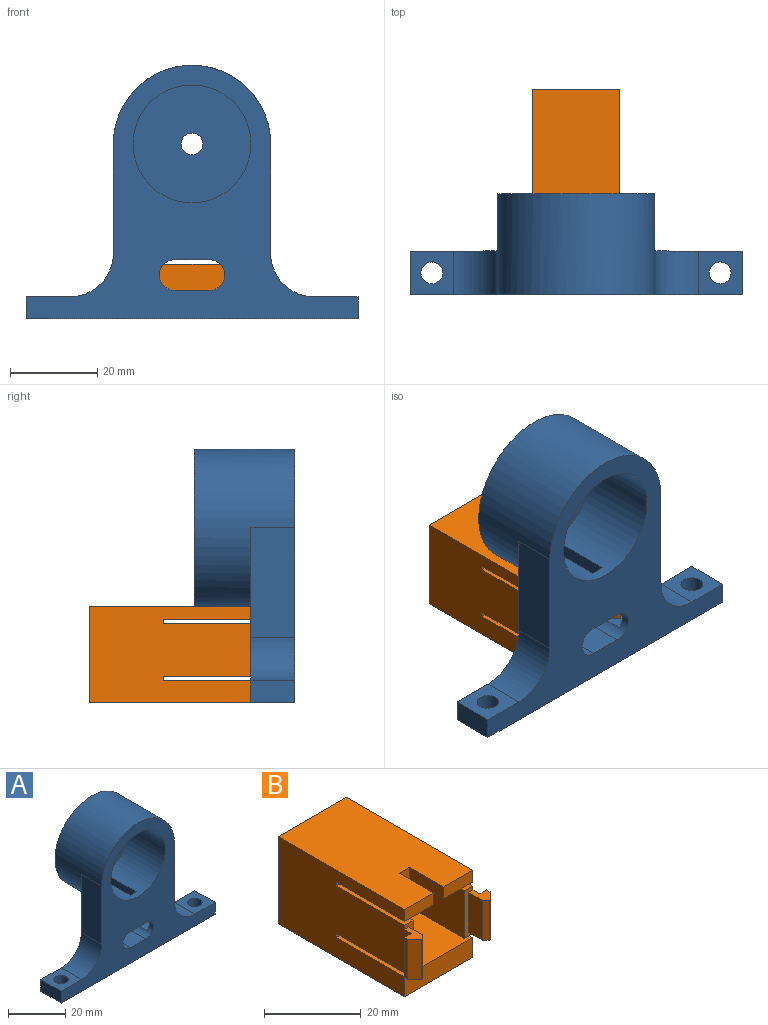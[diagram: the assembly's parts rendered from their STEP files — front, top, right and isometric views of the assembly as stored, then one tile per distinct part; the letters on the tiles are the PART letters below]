
ASSEMBLY  parts=2 mates=1
PART A: 45 faces, bbox 76x23x58 mm
  f0: plane 12.06x6mm, normal (1,0,0), area 72.4mm2, adj f1,f31,f33,f42
  f1: plane 8x5.5mm, normal (0,0,-1), area 42.5mm2, adj f0,f3,f32,f33,f42,f43,f44
  f2: plane 8x5.5mm, normal (0,0,1), area 42.5mm2, adj f3,f34,f37,f38,f39,f40,f41
  f3: plane 76x40mm, normal (0,1,0), area 951.5mm2, adj f1,f2,f4,f5,f6,f7,f8,f9
  f4: plane 76x10mm, normal (0,0,-1), area 720.7mm2, adj f3,f5,f15,f16,f26,f27
  f5: plane 10x5mm, normal (1,0,0), area 50mm2, adj f3,f4,f6,f16
  f6: plane 10x10mm, normal (0,0,1), area 80.4mm2, adj f3,f5,f16,f27,f28
  f7: plane 25x10mm, normal (1,0,0), area 250mm2, adj f3,f16,f17,f28
  f8: plane 25x10mm, normal (-1,0,0), area 250mm2, adj f3,f16,f17,f29
  f9: plane 10x10mm, normal (0,0,1), area 80.4mm2, adj f3,f15,f16,f26,f29
  f10: cylinder r=3.5mm len=10mm, axis (0,-1,0), area 68.4mm2, adj f3,f11,f13,f16,f30,f32,f33
  f11: plane 10x8mm, normal (0,0,-1), area 80mm2, adj f3,f10,f12,f16
  f12: cylinder r=3.5mm len=10mm, axis (0,-1,0), area 68.4mm2, adj f3,f11,f13,f16,f34,f35,f38
  f13: plane 10x7.64mm, normal (0,0,1), area 76.4mm2, adj f3,f10,f12,f16
  f14: cylinder r=13.5mm len=27mm, axis (0,-1,0), area 1481.7mm2, adj f16,f18,f20,f21,f22,f23
  f15: plane 10x5mm, normal (-1,0,0), area 50mm2, adj f3,f4,f9,f16
  f16: plane 76x58mm, normal (0,-1,0), area 1524.9mm2, adj f4,f5,f6,f7,f8,f9,f10,f11
  f17: cylinder r=18mm len=36mm, axis (0,1,0), area 2013.2mm2, adj f3,f7,f8,f16,f20,f21,f22,f24
  f18: plane 5.27x3mm, normal (0,1,0), area 15.6mm2, adj f14,f19,f20,f21
  f19: plane 7.5x3mm, normal (0,0,1), area 22.5mm2, adj f3,f18,f20,f21
  f20: plane 15x5.27mm, normal (-1,0,0), area 73.4mm2, adj f3,f14,f17,f18,f19,f22
  f21: plane 15x5.27mm, normal (1,0,0), area 73.4mm2, adj f3,f14,f17,f18,f19,f22
  f22: plane 4.58x3mm, normal (0,-1,0), area 13.5mm2, adj f14,f17,f20,f21
  f23: plane 27x27mm, normal (0,-1,0), area 552.9mm2, adj f14,f25
  f24: plane 36x36mm, normal (0,1,0), area 998.2mm2, adj f17,f25
  f25: cylinder r=2.5mm len=5mm, axis (0,1,0), area 78.5mm2, adj f23,f24
  f26: cylinder r=2.5mm len=5mm, axis (0,0,1), area 78.5mm2, adj f4,f9
  f27: cylinder r=2.5mm len=5mm, axis (0,0,1), area 78.5mm2, adj f4,f6
  f28: cylinder r=10mm len=10mm, axis (0,-1,0), area 157.1mm2, adj f3,f6,f7,f16
  f29: cylinder r=10mm len=10mm, axis (0,-1,0), area 157.1mm2, adj f3,f8,f9,f16
  f30: plane 8x1.55mm, normal (-1,0,0), area 12.4mm2, adj f3,f10,f31,f33
  f31: plane 8x5.5mm, normal (0,0,1), area 42.5mm2, adj f0,f3,f30,f33,f42,f43,f44
  f32: plane 8x5.61mm, normal (-1,0,0), area 44.9mm2, adj f1,f3,f10,f33
  f33: plane 12.06x5.5mm, normal (0,1,0), area 63mm2, adj f0,f1,f10,f30,f31,f32
  f34: plane 8x1.55mm, normal (1,0,0), area 12.4mm2, adj f2,f3,f12,f38
  f35: plane 8x5.61mm, normal (1,0,0), area 44.9mm2, adj f3,f12,f36,f38
  f36: plane 8x5.5mm, normal (0,0,-1), area 42.5mm2, adj f3,f35,f37,f38,f39,f40,f41
  f37: plane 12.06x6mm, normal (-1,0,0), area 72.4mm2, adj f2,f36,f38,f39
  f38: plane 12.06x5.5mm, normal (0,1,0), area 63mm2, adj f2,f12,f34,f35,f36,f37
  f39: plane 12.06x1mm, normal (0,-1,0), area 12.1mm2, adj f2,f36,f37,f40
  f40: plane 12.06x1mm, normal (-1,0,0), area 12.1mm2, adj f2,f36,f39,f41
  f41: plane 12.06x1mm, normal (-0.71,0.71,0), area 17.1mm2, adj f2,f3,f36,f40
  f42: plane 12.06x1mm, normal (0,-1,0), area 12.1mm2, adj f0,f1,f31,f43
  f43: plane 12.06x1mm, normal (1,0,0), area 12.1mm2, adj f1,f31,f42,f44
  f44: plane 12.06x1mm, normal (0.71,0.71,0), area 17.1mm2, adj f1,f3,f31,f43
PART B: 46 faces, bbox 24x42x22.1 mm
  f0: plane 35x14.06mm, normal (1,0,0), area 452.2mm2, adj f4,f20,f23,f24,f35,f36,f38,f39
  f1: plane 39x22.06mm, normal (-1,0,0), area 796.4mm2, adj f4,f7,f12,f21,f22,f23,f24,f25
  f2: plane 39x22.06mm, normal (1,0,0), area 796.4mm2, adj f5,f6,f15,f21,f22,f23,f24,f25
  f3: plane 35x14.06mm, normal (-1,0,0), area 452.2mm2, adj f5,f20,f23,f24,f40,f41,f43,f44
  f4: plane 12.06x2.5mm, normal (0,-1,0), area 17.6mm2, adj f0,f1,f8,f34,f36,f37,f39
  f5: plane 12.06x2.5mm, normal (0,-1,0), area 17.6mm2, adj f2,f3,f10,f41,f42,f44,f45
  f6: plane 8.5x3mm, normal (0,-1,0), area 25.5mm2, adj f2,f22,f23,f29
  f7: plane 8.5x3mm, normal (0,-1,0), area 25.5mm2, adj f1,f22,f23,f27
  f8: plane 10.06x4mm, normal (1,0,0), area 40.3mm2, adj f4,f19,f34,f37
  f9: plane 10.06x0.25mm, normal (0,-1,0), area 2.5mm2, adj f14,f19,f34,f37
  f10: plane 10.06x4mm, normal (-1,0,0), area 40.3mm2, adj f5,f18,f42,f45
  f11: plane 10.06x0.25mm, normal (0,-1,0), area 2.5mm2, adj f17,f18,f42,f45
  f12: plane 10.06x2mm, normal (0,1,0), area 20.1mm2, adj f1,f13,f34,f37
  f13: plane 10.06x1mm, normal (-1,0,0), area 10.1mm2, adj f12,f14,f34,f37
  f14: plane 10.06x2mm, normal (-0.71,-0.71,0), area 28.5mm2, adj f9,f13,f34,f37
  f15: plane 10.06x2mm, normal (0,1,0), area 20.1mm2, adj f2,f16,f42,f45
  f16: plane 10.06x1mm, normal (1,0,0), area 10.1mm2, adj f15,f17,f42,f45
  f17: plane 10.06x2mm, normal (0.71,-0.71,0), area 28.5mm2, adj f11,f16,f42,f45
  f18: plane 10.06x1mm, normal (-0.71,-0.71,0), area 14.2mm2, adj f10,f11,f42,f45
  f19: plane 10.06x1mm, normal (0.71,-0.71,0), area 14.2mm2, adj f8,f9,f34,f37
  f20: plane 15x14.06mm, normal (0,-1,0), area 145.9mm2, adj f0,f3,f23,f24,f30,f31,f32,f33
  f21: plane 22.06x20mm, normal (0,1,0), area 376.3mm2, adj f1,f2,f22,f25,f30,f31,f32,f33
  f22: plane 37x20mm, normal (0,0,1), area 710mm2, adj f1,f2,f6,f7,f21,f27,f28,f29
  f23: plane 35x20mm, normal (0,0,-1), area 595mm2, adj f0,f1,f2,f3,f6,f7,f20,f27
  f24: plane 35x20mm, normal (0,0,1), area 625mm2, adj f0,f1,f2,f3,f20,f26,f35,f40
  f25: plane 37x20mm, normal (0,0,-1), area 740mm2, adj f1,f2,f21,f26
  f26: plane 20x5mm, normal (0,-1,0), area 100mm2, adj f1,f2,f24,f25
  f27: plane 10x3mm, normal (1,0,0), area 30mm2, adj f7,f22,f23,f28
  f28: plane 3x3mm, normal (0,-1,0), area 9mm2, adj f22,f23,f27,f29
  f29: plane 10x3mm, normal (-1,0,0), area 30mm2, adj f6,f22,f23,f28
  f30: plane 13x2mm, normal (0,0,1), area 26mm2, adj f20,f21,f31,f33
  f31: plane 5x2mm, normal (1,0,0), area 10mm2, adj f20,f21,f30,f32
  f32: plane 13x2mm, normal (0,0,-1), area 26mm2, adj f20,f21,f31,f33
  f33: plane 5x2mm, normal (-1,0,0), area 10mm2, adj f20,f21,f30,f32
  f34: plane 5x3.25mm, normal (0,0,-1), area 9.8mm2, adj f1,f4,f8,f9,f12,f13,f14,f19
  f35: plane 2.5x1mm, normal (0,-1,0), area 2.5mm2, adj f0,f1,f24,f36
  f36: plane 20x2.5mm, normal (0,0,-1), area 50mm2, adj f0,f1,f4,f35
  f37: plane 5x3.25mm, normal (0,0,1), area 9.8mm2, adj f1,f4,f8,f9,f12,f13,f14,f19
  f38: plane 2.5x1mm, normal (0,-1,0), area 2.5mm2, adj f0,f1,f23,f39
  f39: plane 20x2.5mm, normal (0,0,1), area 50mm2, adj f0,f1,f4,f38
  f40: plane 2.5x1mm, normal (0,-1,0), area 2.5mm2, adj f2,f3,f24,f41
  f41: plane 20x2.5mm, normal (0,0,-1), area 50mm2, adj f2,f3,f5,f40
  f42: plane 5x3.25mm, normal (0,0,-1), area 9.7mm2, adj f2,f5,f10,f11,f15,f16,f17,f18
  f43: plane 2.5x1mm, normal (0,-1,0), area 2.5mm2, adj f2,f3,f23,f44
  f44: plane 20x2.5mm, normal (0,0,1), area 50mm2, adj f2,f3,f5,f43
  f45: plane 5x3.25mm, normal (0,0,1), area 9.7mm2, adj f2,f5,f10,f11,f15,f16,f17,f18
PLACE A t=(-41.58,-9.93,9.37)mm
PLACE B t=(-41.58,-9.93,9.37)mm
MATE fastened B.f15 <-> A.f39  axis (0,1,0) through (-29.58,-1.93,21.4)mm
